# Revit family: Kreuzung_horizontal_Russia
name_source: partatom
category: Generic Models
revit_build: Autodesk Revit 2015 (Build: 20140606_1530(x64)
units: mm (PartAtom-declared; Revit-internal decimal feet)

## types (7) — shared parameters
Manufacturer = OBO Bettermann
Material = Steel, Galvanized
URL = http://www.obo-bettermann.com

## per-type parameters (varying)
| type | A | Article Type | B | GTIN | Manufacturer Art. No. |
| RK 610 FS RU | 98 mm  [stored 0.321522 ft] | RK 610 FS RU | 198 mm  [stored 0.649606 ft] | 4012196626205 | 6043652 |
| RK 615 FS RU | 148 mm  [stored 0.485564 ft] | RK 615 FS RU | 248 mm  [stored 0.813648 ft] | 4012196649365 | 6043653 |
| RK 620 FS RU | 198 mm  [stored 0.649606 ft] | RK 620 FS RU | 298 mm  [stored 0.97769 ft] | 4012196626212 | 6043654 |
| RK 630 FS RU | 298 mm  [stored 0.97769 ft] | RK 630 FS RU | 398 mm  [stored 1.30577 ft] | 4012196626229 | 6043656 |
| RK 640 FS RU | 398 mm  [stored 1.30577 ft] | RK 640 FS RU | 498 mm  [stored 1.63386 ft] | 4012196626236 | 6043660 |
| RK 650 FS RU | 498 mm  [stored 1.63386 ft] | DFK 500 FS RU | 598 mm  [stored 1.96194 ft] | 4012196626243 | 6043662 |
| RK 660 FS RU | 598 mm  [stored 1.96194 ft] | RK 660 FS RU | 698 mm  [stored 2.29003 ft] | 4012196626250 | 6043664 |

note: [stored X ft] marks values corroborated as IEEE doubles in the binary element streams (Revit-internal decimal feet)

## geometry (parser evidence)
native form markers: Sweep x2
no freeform markers — native parametric forms only
